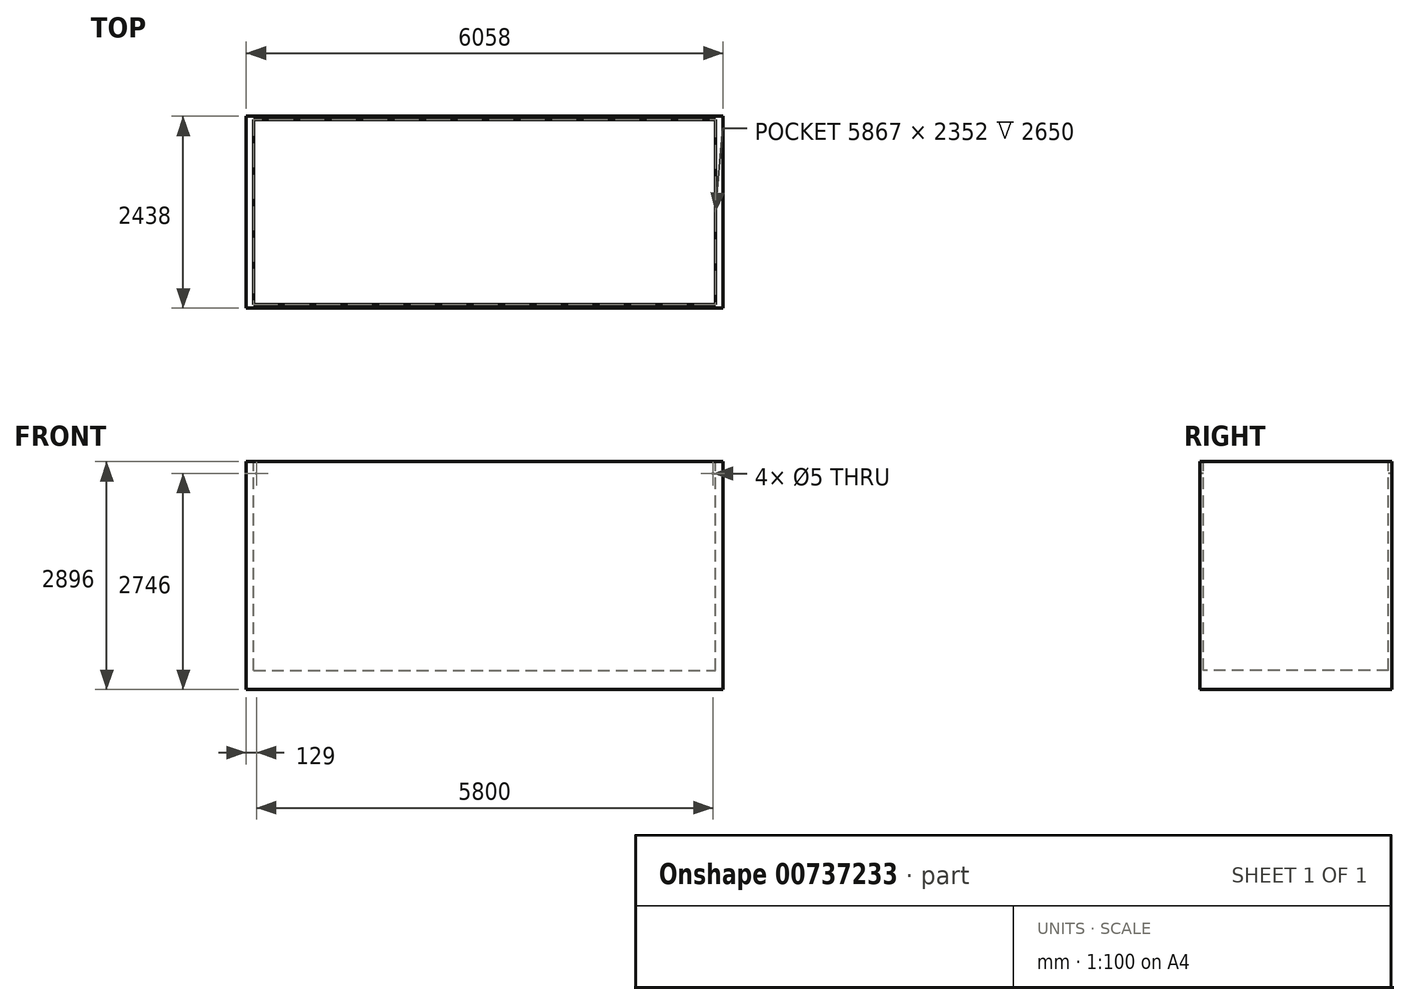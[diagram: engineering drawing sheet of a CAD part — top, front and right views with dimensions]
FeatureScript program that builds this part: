
annotation { "Feature Type Name" : "Feature", "Feature Type Description" : "" }
export const myFeature = defineFeature(function(context is Context, id is Id, definition is map)
    precondition{}
    {
        {
            var Q0;
            Q0=qCreatedBy(makeId("Top.planeOp"),FACE);
            var sketch = newSketch(context, id + "F0", { "sketchPlane" : qUnion([Q0])});
            skLineSegment(sketch, "E0.bottom", {"start": v(0, 0) * mm, "end": v(6058, 0) * mm});
            skLineSegment(sketch, "E0.top", {"start": v(0, 2438) * mm, "end": v(6058, 2438) * mm});
            skLineSegment(sketch, "E0.left", {"start": v(0, 0) * mm, "end": v(0, 2438) * mm});
            skLineSegment(sketch, "E0.right", {"start": v(6058, 0) * mm, "end": v(6058, 2438) * mm});
            skSolve(sketch);
        }
        {
            var Q0;
            Q0=makeQuery(id+"F0.imprint","IMPRINT",FACE,{"disambiguationData":[TD([[makeQuery(id+"F0.imprint","IMPRINT",EDGE,{"derivedFrom":sQuery(id+"F0.wireOp",EDGE,"E0.bottom")}),1.0]])]});
            extrude(context, id + "F1", {"entities" : qUnion([Q0]), "depth" : 2896 * mm, "offsetDistance" : 25 * mm});
        }
        {
            var Q0;
            Q0=makeQuery(id+"F1.opExtrude","CAP_FACE",FACE,{"disambiguationData":[OSD([sQuery(id+"F0.wireOp",EDGE,"E0.bottom"),sQuery(id+"F0.wireOp",EDGE,"E0.top"),sQuery(id+"F0.wireOp",EDGE,"E0.left"),sQuery(id+"F0.wireOp",EDGE,"E0.right")])],"isStart":false});
            var sketch = newSketch(context, id + "F2", { "sketchPlane" : qUnion([Q0])});
            skLineSegment(sketch, "E1.bottom", {"start": v(95.5, 2395) * mm, "end": v(5962.5, 2395) * mm});
            skLineSegment(sketch, "E1.top", {"start": v(95.5, 43) * mm, "end": v(5962.5, 43) * mm});
            skLineSegment(sketch, "E1.left", {"start": v(95.5, 2395) * mm, "end": v(95.5, 43) * mm});
            skLineSegment(sketch, "E1.right", {"start": v(5962.5, 2395) * mm, "end": v(5962.5, 43) * mm});
            skLineSegment(sketch, "E2", {"start": v(95.5, 1219) * mm, "end": v(0, 1219) * mm});
            skLineSegment(sketch, "E3", {"start": v(5962.5, 1219) * mm, "end": v(6058, 1219) * mm});
            skLineSegment(sketch, "E4", {"start": v(3029, 2395) * mm, "end": v(3029, 2438) * mm});
            skLineSegment(sketch, "E5", {"start": v(3029, 43) * mm, "end": v(3029, 0) * mm});
            skSolve(sketch);
        }
        {
            var Q0;
            {var subQ4=sQuery(id+"F2.wireOp",EDGE,"E1.left");var subQ6=sQuery(id+"F2.wireOp",EDGE,"E1.bottom");var subQ9=makeQuery(id+"F2.imprint","INTERSECT",VERTEX,{"derivedFrom":[subQ6,subQ4]});Q0=makeQuery(id+"F2.imprint","IMPRINT",FACE,{"disambiguationData":[TD([[makeQuery(id+"F2.imprint","IMPRINT",EDGE,{"disambiguationData":[TD([[subQ9,-1.0]])],"derivedFrom":subQ6}),-1.0]])]});}
            extrude(context, id + "F3", {"entities" : qUnion([Q0]), "operationType" : NewBodyOperationType.REMOVE, "oppositeDirection" : true, "depth" : 2650 * mm, "offsetDistance" : 25 * mm});
        }
        {
            var Q0;
            Q0=makeQuery(id+"F1.opExtrude","SWEPT_FACE",FACE,{"disambiguationData":[OSD([sQuery(id+"F0.wireOp",EDGE,"E0.bottom")])]});
            var sketch = newSketch(context, id + "F4", { "sketchPlane" : qUnion([Q0])});
            skLineSegment(sketch, "E6", {"start": v(129, 2746) * mm, "end": v(5929, 2746) * mm});
            skLineSegment(sketch, "E7", {"start": v(129, 2746) * mm, "end": v(0, 2746) * mm});
            skLineSegment(sketch, "E8", {"start": v(5929, 2746) * mm, "end": v(6058, 2746) * mm});
            skCircle(sketch, "E9", {"center": v(129, 2746) * mm, "radius": 2.5 * mm});
            skCircle(sketch, "E10", {"center": v(5929, 2746) * mm, "radius": 2.5 * mm});
            skSolve(sketch);
        }
        {
            var Q0;
            {var subQ0=sQuery(id+"F4.wireOp",EDGE,"E7");var subQ1=sQuery(id+"F4.wireOp",EDGE,"E6");var subQ2=makeQuery(id+"F4.imprint","INTERSECT",VERTEX,{"derivedFrom":[subQ1,subQ0]});Q0=makeQuery(id+"F4.imprint","IMPRINT",FACE,{"disambiguationData":[TD([[makeQuery(id+"F4.imprint","IMPRINT",EDGE,{"disambiguationData":[TD([[subQ2,-1.0]])],"derivedFrom":subQ1}),-1.0]])]});}
            var Q1;
            {var subQ0=sQuery(id+"F4.wireOp",EDGE,"E7");var subQ1=sQuery(id+"F4.wireOp",EDGE,"E6");var subQ2=makeQuery(id+"F4.imprint","INTERSECT",VERTEX,{"derivedFrom":[subQ1,subQ0]});Q1=makeQuery(id+"F4.imprint","IMPRINT",FACE,{"disambiguationData":[TD([[makeQuery(id+"F4.imprint","IMPRINT",EDGE,{"disambiguationData":[TD([[subQ2,-1.0]])],"derivedFrom":subQ1}),1.0]])]});}
            var Q2;
            {var subQ0=sQuery(id+"F4.wireOp",EDGE,"E8");var subQ1=sQuery(id+"F4.wireOp",EDGE,"E6");var subQ2=makeQuery(id+"F4.imprint","INTERSECT",VERTEX,{"derivedFrom":[subQ1,subQ0]});Q2=makeQuery(id+"F4.imprint","IMPRINT",FACE,{"disambiguationData":[TD([[makeQuery(id+"F4.imprint","IMPRINT",EDGE,{"disambiguationData":[TD([[subQ2,1.0]])],"derivedFrom":subQ1}),-1.0]])]});}
            var Q3;
            {var subQ0=sQuery(id+"F4.wireOp",EDGE,"E8");var subQ1=sQuery(id+"F4.wireOp",EDGE,"E6");var subQ2=makeQuery(id+"F4.imprint","INTERSECT",VERTEX,{"derivedFrom":[subQ1,subQ0]});Q3=makeQuery(id+"F4.imprint","IMPRINT",FACE,{"disambiguationData":[TD([[makeQuery(id+"F4.imprint","IMPRINT",EDGE,{"disambiguationData":[TD([[subQ2,1.0]])],"derivedFrom":subQ1}),1.0]])]});}
            extrude(context, id + "F5", {"entities" : qUnion([Q0, Q1, Q2, Q3]), "operationType" : NewBodyOperationType.REMOVE, "endBound" : BoundingType.THROUGH_ALL, "oppositeDirection" : true, "depth" : 25 * mm, "offsetDistance" : 25 * mm});
        }
    });
